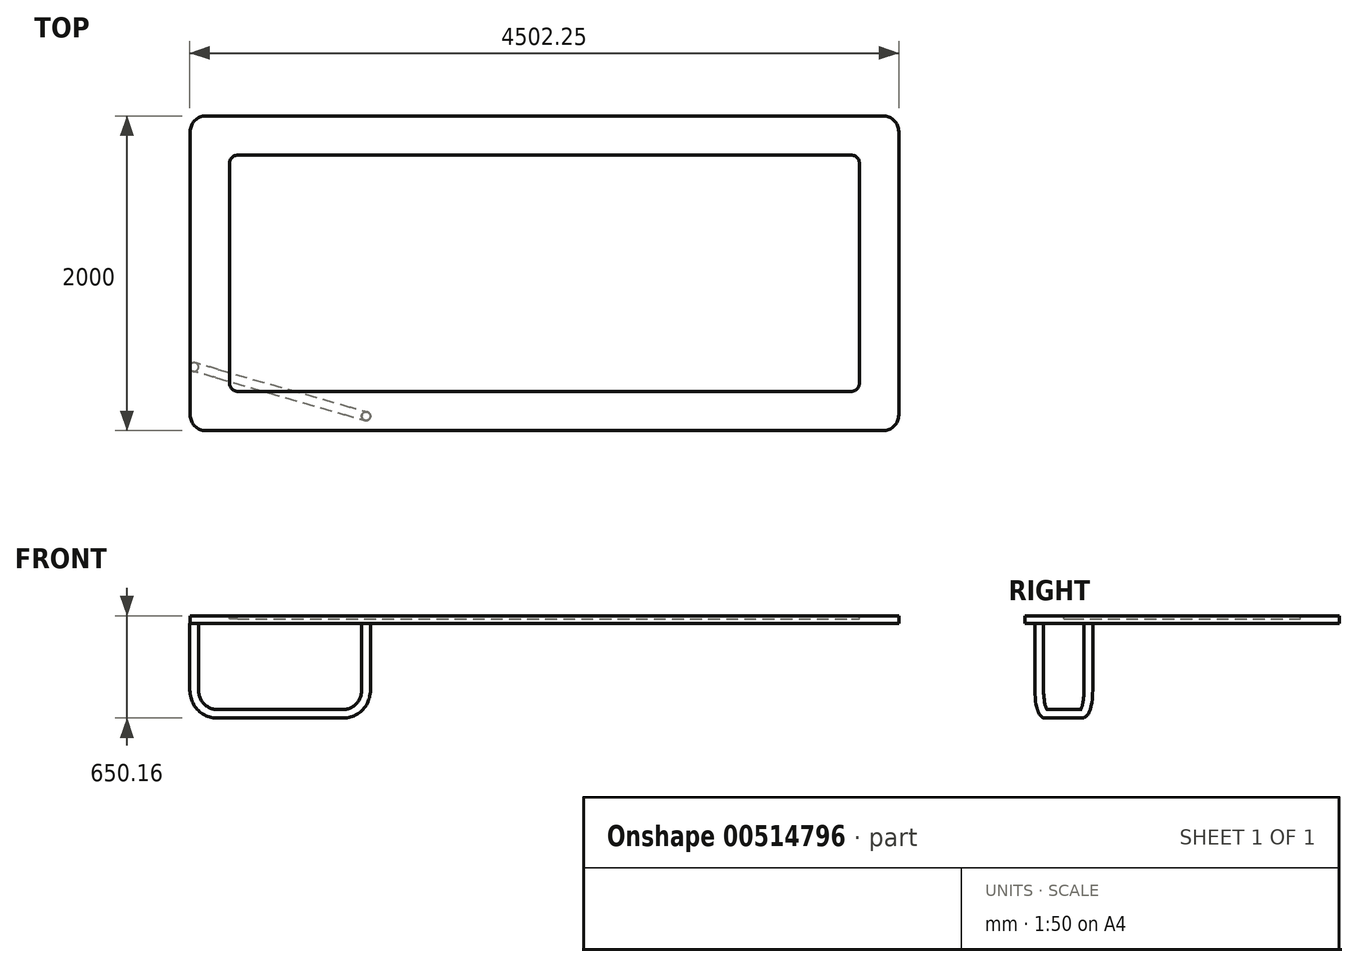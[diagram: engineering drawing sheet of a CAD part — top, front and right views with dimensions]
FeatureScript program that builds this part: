
annotation { "Feature Type Name" : "Feature", "Feature Type Description" : "" }
export const myFeature = defineFeature(function(context is Context, id is Id, definition is map)
    precondition{}
    {
        {
            var Q0;
            Q0=qCreatedBy(makeId("Top.planeOp"),FACE);
            var sketch = newSketch(context, id + "F0", { "sketchPlane" : qUnion([Q0])});
            skLineSegment(sketch, "E0.bottom", {"start": v(2250, -1000) * mm, "end": v(-2250, -1000) * mm});
            skLineSegment(sketch, "E0.top", {"start": v(2250, 1000) * mm, "end": v(-2250, 1000) * mm});
            skLineSegment(sketch, "E0.left", {"start": v(2250, -1000) * mm, "end": v(2250, 1000) * mm});
            skLineSegment(sketch, "E0.right", {"start": v(-2250, -1000) * mm, "end": v(-2250, 1000) * mm});
            skPoint(sketch, "E0.middle", {"position": v(0, 0) * mm});
            skLineSegment(sketch, "E1", {"start": v(-500, 1000) * mm, "end": v(-500, -1000) * mm, "construction": true});
            skLineSegment(sketch, "E2", {"start": v(500, 1000) * mm, "end": v(500, -1000) * mm, "construction": true});
            skLineSegment(sketch, "E3", {"start": v(-2250, 500) * mm, "end": v(2250, 500) * mm, "construction": true});
            skLineSegment(sketch, "E4", {"start": v(-2250, -500) * mm, "end": v(2250, -500) * mm, "construction": true});
            skLineSegment(sketch, "E5", {"start": v(-2250, -500) * mm, "end": v(-500, -1000) * mm, "construction": true});
            skSolve(sketch);
        }
        {
            var Q0;
            Q0=makeQuery(id+"F0.imprint","IMPRINT",FACE,{"disambiguationData":[TD([[makeQuery(id+"F0.imprint","IMPRINT",EDGE,{"derivedFrom":sQuery(id+"F0.wireOp",EDGE,"E0.bottom")}),-1.0]])]});
            extrude(context, id + "F1", {"entities" : qUnion([Q0]), "depth" : 50 * mm, "offsetDistance" : 25.4 * mm});
        }
        {
            var Q0;
            Q0=makeQuery(id+"F1.opExtrude","CAP_FACE",FACE,{"disambiguationData":[OSD([sQuery(id+"F0.wireOp",EDGE,"E0.bottom"),sQuery(id+"F0.wireOp",EDGE,"E0.top"),sQuery(id+"F0.wireOp",EDGE,"E0.left"),sQuery(id+"F0.wireOp",EDGE,"E0.right")])],"isStart":false});
            var sketch = newSketch(context, id + "F2", { "sketchPlane" : qUnion([Q0])});
            skLineSegment(sketch, "E6.0", {"start": v(2000, -750) * mm, "end": v(2000, 750) * mm});
            skLineSegment(sketch, "E6.1", {"start": v(-2000, -750) * mm, "end": v(2000, -750) * mm});
            skLineSegment(sketch, "E6.2", {"start": v(-2000, 750) * mm, "end": v(-2000, -750) * mm});
            skLineSegment(sketch, "E6.3", {"start": v(2000, 750) * mm, "end": v(-2000, 750) * mm});
            skSolve(sketch);
        }
        {
            var Q0;
            Q0=makeQuery(id+"F2.imprint","IMPRINT",FACE,{"disambiguationData":[TD([[makeQuery(id+"F2.imprint","IMPRINT",EDGE,{"derivedFrom":sQuery(id+"F2.wireOp",EDGE,"E6.0")}),1.0]])]});
            extrude(context, id + "F3", {"entities" : qUnion([Q0]), "operationType" : NewBodyOperationType.REMOVE, "oppositeDirection" : true, "depth" : 20 * mm, "offsetDistance" : 25.4 * mm});
        }
        {
            var Q0;
            Q0=makeQuery(id+"F1.opExtrude","SWEPT_EDGE",EDGE,{"disambiguationData":[OSD([sQuery(id+"F0.wireOp",EDGE,"E0.bottom"),sQuery(id+"F0.wireOp",EDGE,"E0.right")])]});
            var Q1;
            Q1=makeQuery(id+"F1.opExtrude","SWEPT_EDGE",EDGE,{"disambiguationData":[OSD([sQuery(id+"F0.wireOp",EDGE,"E0.bottom"),sQuery(id+"F0.wireOp",EDGE,"E0.left")])]});
            var Q2;
            Q2=makeQuery(id+"F1.opExtrude","SWEPT_EDGE",EDGE,{"disambiguationData":[OSD([sQuery(id+"F0.wireOp",EDGE,"E0.top"),sQuery(id+"F0.wireOp",EDGE,"E0.left")])]});
            var Q3;
            Q3=makeQuery(id+"F1.opExtrude","SWEPT_EDGE",EDGE,{"disambiguationData":[OSD([sQuery(id+"F0.wireOp",EDGE,"E0.top"),sQuery(id+"F0.wireOp",EDGE,"E0.right")])]});
            fillet(context, id + "F4", {"entities" : qUnion([Q0, Q1, Q2, Q3]), "radius" : 100 * mm, "tangentPropagation" : true, "allowEdgeOverflow" : false});
        }
        {
            var Q0;
            Q0=makeQuery(id+"F3.boolean.opBoolean","COPY",EDGE,{"derivedFrom":makeQuery(id+"F3.opExtrude","SWEPT_EDGE",EDGE,{"disambiguationData":[OSD([sQuery(id+"F4Uw2HM8OT02xsG_1.wireOp",EDGE,"560c6e82-6e68-4b31-875d-84cad3cc388a.1"),sQuery(id+"F4Uw2HM8OT02xsG_1.wireOp",EDGE,"560c6e82-6e68-4b31-875d-84cad3cc388a.2")])]})});
            var Q1;
            Q1=makeQuery(id+"F3.boolean.opBoolean","COPY",EDGE,{"derivedFrom":makeQuery(id+"F3.opExtrude","SWEPT_EDGE",EDGE,{"disambiguationData":[OSD([sQuery(id+"F4Uw2HM8OT02xsG_1.wireOp",EDGE,"560c6e82-6e68-4b31-875d-84cad3cc388a.2"),sQuery(id+"F4Uw2HM8OT02xsG_1.wireOp",EDGE,"560c6e82-6e68-4b31-875d-84cad3cc388a.3")])]})});
            var Q2;
            Q2=makeQuery(id+"F3.boolean.opBoolean","COPY",EDGE,{"derivedFrom":makeQuery(id+"F3.opExtrude","SWEPT_EDGE",EDGE,{"disambiguationData":[OSD([sQuery(id+"F4Uw2HM8OT02xsG_1.wireOp",EDGE,"560c6e82-6e68-4b31-875d-84cad3cc388a.0"),sQuery(id+"F4Uw2HM8OT02xsG_1.wireOp",EDGE,"560c6e82-6e68-4b31-875d-84cad3cc388a.3")])]})});
            var Q3;
            Q3=makeQuery(id+"F3.boolean.opBoolean","COPY",EDGE,{"derivedFrom":makeQuery(id+"F3.opExtrude","SWEPT_EDGE",EDGE,{"disambiguationData":[OSD([sQuery(id+"F4Uw2HM8OT02xsG_1.wireOp",EDGE,"560c6e82-6e68-4b31-875d-84cad3cc388a.0"),sQuery(id+"F4Uw2HM8OT02xsG_1.wireOp",EDGE,"560c6e82-6e68-4b31-875d-84cad3cc388a.1")])]})});
            var Q4;
            Q4=makeQuery(id+"F3.boolean.opBoolean","COPY",EDGE,{"derivedFrom":makeQuery(id+"F3.opExtrude","SWEPT_EDGE",EDGE,{"disambiguationData":[OSD([sQuery(id+"F2.wireOp",EDGE,"E6.2"),sQuery(id+"F2.wireOp",EDGE,"E6.3")])]})});
            var Q5;
            Q5=makeQuery(id+"F3.boolean.opBoolean","COPY",EDGE,{"derivedFrom":makeQuery(id+"F3.opExtrude","SWEPT_EDGE",EDGE,{"disambiguationData":[OSD([sQuery(id+"F2.wireOp",EDGE,"E6.1"),sQuery(id+"F2.wireOp",EDGE,"E6.2")])]})});
            var Q6;
            Q6=makeQuery(id+"F3.boolean.opBoolean","COPY",EDGE,{"derivedFrom":makeQuery(id+"F3.opExtrude","SWEPT_EDGE",EDGE,{"disambiguationData":[OSD([sQuery(id+"F2.wireOp",EDGE,"E6.0"),sQuery(id+"F2.wireOp",EDGE,"E6.3")])]})});
            var Q7;
            Q7=makeQuery(id+"F3.boolean.opBoolean","COPY",EDGE,{"derivedFrom":makeQuery(id+"F3.opExtrude","SWEPT_EDGE",EDGE,{"disambiguationData":[OSD([sQuery(id+"F2.wireOp",EDGE,"E6.0"),sQuery(id+"F2.wireOp",EDGE,"E6.1")])]})});
            fillet(context, id + "F5", {"entities" : qUnion([Q0, Q1, Q2, Q3, Q4, Q5, Q6, Q7]), "radius" : 50 * mm, "tangentPropagation" : true, "allowEdgeOverflow" : false});
        }
        {
            var Q0;
            Q0=sQuery(id+"F0.wireOp",EDGE,"E1");
            cPlane(context, id + "F6", {"entities" : qUnion([Q0]), "cplaneType" : CPlaneType.LINE_ANGLE, "offset" : 25 * mm, "angle" : 90 * degree, "width" : 150 * mm, "height" : 150 * mm});
        }
        {
            var Q0;
            Q0=sQuery(id+"F0.wireOp",EDGE,"E5");
            cPlane(context, id + "F7", {"entities" : qUnion([Q0]), "cplaneType" : CPlaneType.LINE_ANGLE, "offset" : 25 * mm, "angle" : 0 * degree, "width" : 150 * mm, "height" : 150 * mm});
        }
        {
            var Q0;
            Q0=qCreatedBy(id+"F7.planeOp",FACE);
            var sketch = newSketch(context, id + "F8", { "sketchPlane" : qUnion([Q0])});
            skPoint(sketch, "E7", {"position": v(2026.07, 0) * mm});
            skPoint(sketch, "E8", {"position": v(789, 0) * mm});
            skLineSegment(sketch, "E9", {"start": v(2026.07, 0) * mm, "end": v(2026.07, -423.2) * mm});
            skLineSegment(sketch, "E10", {"start": v(1826.07, -623.2) * mm, "end": v(989.75, -623.2) * mm});
            skLineSegment(sketch, "E11", {"start": v(789.75, -423.56) * mm, "end": v(789, 0) * mm});
            skPoint(sketch, "E12.visualSharp", {"position": v(2026.07, -623.2) * mm});
            skArc(sketch, "E12.filletArc", {"start": v(1826.07, -623.2) * mm, "mid": v(1967.49, -564.63) * mm, "end": v(2026.07, -423.2) * mm});
            skPoint(sketch, "E13.visualSharp", {"position": v(790.1, -623.2) * mm});
            skArc(sketch, "E13.filletArc", {"start": v(789.75, -423.56) * mm, "mid": v(848.45, -564.75) * mm, "end": v(989.75, -623.2) * mm});
            skSolve(sketch);
        }
        {
            var Q0;
            Q0=makeQuery(id+"F0.imprint","IMPRINT",FACE,{"disambiguationData":[TD([[makeQuery(id+"F0.imprint","IMPRINT",EDGE,{"derivedFrom":sQuery(id+"F0.wireOp",EDGE,"E0.bottom")}),-1.0]])]});
            var sketch = newSketch(context, id + "F9", { "sketchPlane" : qUnion([Q0])});
            skCircle(sketch, "E14", {"center": v(-2224.65, -595.64) * mm, "radius": 27.6 * mm});
            skPoint(sketch, "E14.first.point", {"position": v(-2251.37, -602.58) * mm});
            skPoint(sketch, "E14.second.point", {"position": v(-2199.8, -583.6) * mm});
            skPoint(sketch, "E14.third.point", {"position": v(-2209.04, -618.41) * mm});
            skPoint(sketch, "E15.first.point", {"position": v(-1250.27, -998.51) * mm});
            skSolve(sketch);
        }
        {
            var Q0;
            Q0 = qSketchRegion(id + "F9", true);
            var Q1;
            Q1 = qConstructionFilter(qBodyType(qCreatedBy(id + "F8" ,EDGE), BodyType.WIRE), ConstructionObject.NO);
            sweep(context, id + "F10", {"operationType" : NewBodyOperationType.ADD, "profiles" : qUnion([Q0]), "path" : qUnion([Q1])});
        }
    });
